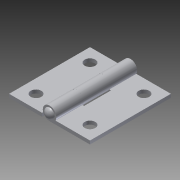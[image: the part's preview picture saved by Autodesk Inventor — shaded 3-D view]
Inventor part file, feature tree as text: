
AUTODESK INVENTOR PART (.ipt)
format: ipt  version: 2014 (Build 180170000, 170)  size: 172,544 bytes
history: native  units: in
note: dims shown in document units (in); Inventor stores cm internally (conversion verified against a paired STEP export)
features: extrude x4, imported_body x3, sketch x2, revolve x1, other x1
ambient origin geometry x8: Origin, YZ Plane, XZ Plane, XY Plane, X Axis, Y Axis, Z Axis, Center Point
bodies: Body1 (feature_tree), Body2 (feature_tree), Body3 (feature_tree)
feature tree (11):
  revolve  "Revolve1"  [1 undecoded]
  other  "1609A1201"
  extrude  "Extrusion1"  Depth=1.0in TaperAngle=0.0deg
  extrude  "Extrusion2"  Depth=1.0in
  extrude  "Extrude4"  Depth=0.25in
  extrude  "Extrude5"  Depth=0.25in
  imported_body  "Base1"
  imported_body  "Base2"
  imported_body  "Base3"
  sketch  "Sketch2"  dims[d0=0.196in d1=0.25in]
  sketch  "Sketch3"  dims[d3=0.25in d4=1.0in d5=0.0in d6=0.196in d7=0.25in d8=0.25in d9=1.0in d10=0.0in]
note: 1 required parameter value undecoded (feature->parameter linkage not recoverable at this tier; creation-order binding heuristic only, values carry confidence <= 0.55)
